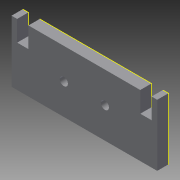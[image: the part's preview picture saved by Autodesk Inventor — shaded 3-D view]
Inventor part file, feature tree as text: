
AUTODESK INVENTOR PART (.ipt)
format: ipt  version: 2015 (Build 190159000, 159)  size: 129,024 bytes
history: native  units: mm
features: sketch x4, extrude x3
ambient origin geometry x8: Origin, YZ Plane, XZ Plane, XY Plane, X Axis, Y Axis, Z Axis, Center Point
bodies: Solid1 (feature_tree)
feature tree (7):
  extrude  "Extrusion1"  Depth=5.5mm TaperAngle=0.0deg
  extrude  "Extrusion2"  Depth=5.5mm
  sketch  "Sketch4"  dims[d7=10.0mm d8=30.0mm]
  extrude  "Extrusion3"  Depth=30.0mm
  sketch  "Sketch1"  dims[d0=71.0mm d1=5.5mm d2=0.0mm]
  sketch  "Sketch3"  dims[d5=30.0mm d6=5.5mm]
  sketch  "Sketch5"  dims[d9=3.0mm d10=0.0mm d11=4.0mm d12=20.0mm d13=10.0mm d14=0.0mm]
